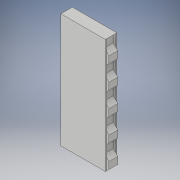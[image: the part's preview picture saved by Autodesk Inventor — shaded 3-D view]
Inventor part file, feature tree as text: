
AUTODESK INVENTOR PART (.ipt)
format: ipt  version: 2017 (Build 210142000, 142)  size: 159,744 bytes
history: native  units: in
note: dims shown in document units (in); Inventor stores cm internally (conversion verified against a paired STEP export)
features: extrude x3, sketch x2
ambient origin geometry x8: Origin, YZ Plane, XZ Plane, XY Plane, X Axis, Y Axis, Z Axis, Center Point
bodies: Solid1 (feature_tree)
feature tree (5):
  extrude  "door"  Depth=9.0in
  sketch  "Sketch2"  dims[d2=0.9in d3=0.0in d7=9.0in d19=0.7in d20=0.0in d21=0.7in d22=0.0in d23=0.25in d24=9.0in d25=0.45in d26=0.45in d27=0.45in d28=0.45in d29=0.45in d30=0.45in d31=0.45in d32=0.45in d33=0.45in d34=45.0deg d35=45.0deg]
  extrude  "teeth cut"  Depth=9.0in
  extrude  "teeth make"  Depth=0.7in TaperAngle=0.0deg
  sketch  "Sketch1"  dims[d0=3.5in d1=9.0in]
